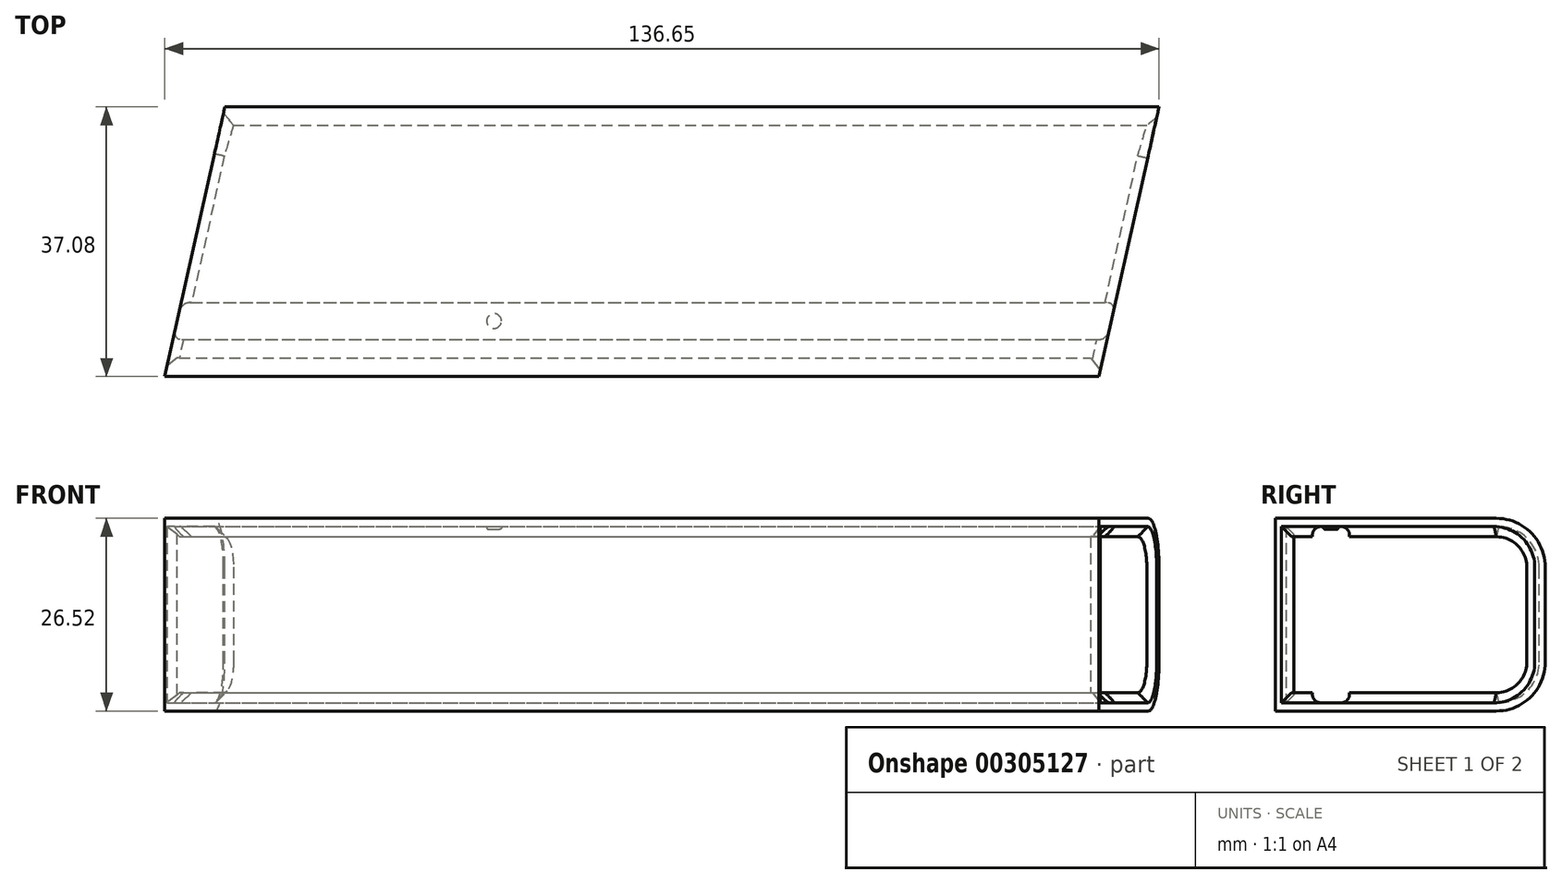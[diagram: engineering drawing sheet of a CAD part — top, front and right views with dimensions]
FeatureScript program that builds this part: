
annotation { "Feature Type Name" : "Feature", "Feature Type Description" : "" }
export const myFeature = defineFeature(function(context is Context, id is Id, definition is map)
    precondition{}
    {
        {
            var Q0;
            Q0=qCreatedBy(makeId("Top.planeOp"),FACE);
            var sketch = newSketch(context, id + "F0", { "sketchPlane" : qUnion([Q0])});
            skLineSegment(sketch, "E0.bottom", {"start": v(0, 0) * mm, "end": v(136.65, 0) * mm});
            skLineSegment(sketch, "E0.top", {"start": v(0, 37.08) * mm, "end": v(136.65, 37.08) * mm});
            skLineSegment(sketch, "E0.left", {"start": v(0, 0) * mm, "end": v(0, 37.08) * mm});
            skLineSegment(sketch, "E0.right", {"start": v(136.65, 0) * mm, "end": v(136.65, 37.08) * mm});
            skSolve(sketch);
        }
        {
            var Q0;
            Q0 = qSketchRegion(id + "F0", true);
            extrude(context, id + "F1", {"entities" : qUnion([Q0]), "depth" : 26.52 * mm});
        }
        {
            var Q0;
            Q0=makeQuery(id+"F1.opExtrude","SWEPT_FACE",FACE,{"disambiguationData":[OSD([sQuery(id+"F0.wireOp",EDGE,"E0.right")])]});
            var Q1;
            Q1=makeQuery(id+"F1.opExtrude","CAP_VERTEX",VERTEX,{"disambiguationData":[OSD([sQuery(id+"F0.wireOp",EDGE,"E0.bottom"),sQuery(id+"F0.wireOp",EDGE,"E0.right")])],"isStart":false});
            cPlane(context, id + "F2", {"entities" : qUnion([Q0, Q1]), "cplaneType" : CPlaneType.PLANE_POINT, "offset" : 25.4 * mm, "width" : 152.4 * mm, "height" : 152.4 * mm});
        }
        {
            var Q0;
            Q0=makeQuery(id+"F1.opExtrude","CAP_FACE",FACE,{"disambiguationData":[OSD([sQuery(id+"F0.wireOp",EDGE,"E0.bottom"),sQuery(id+"F0.wireOp",EDGE,"E0.top"),sQuery(id+"F0.wireOp",EDGE,"E0.left"),sQuery(id+"F0.wireOp",EDGE,"E0.right")])],"isStart":false});
            var sketch = newSketch(context, id + "F3", { "sketchPlane" : qUnion([Q0])});
            skLineSegment(sketch, "E1.0", {"start": v(0, 0) * mm, "end": v(0, 37.08) * mm});
            skLineSegment(sketch, "E2.0", {"start": v(136.65, 0) * mm, "end": v(136.65, 37.08) * mm});
            skLineSegment(sketch, "E3.0", {"start": v(0, 37.08) * mm, "end": v(136.65, 37.08) * mm, "construction": true});
            skLineSegment(sketch, "E4.0", {"start": v(0, 0) * mm, "end": v(136.65, 0) * mm, "construction": true});
            skLineSegment(sketch, "E5", {"start": v(0, 0) * mm, "end": v(8.26, 37.08) * mm});
            skLineSegment(sketch, "E6", {"start": v(8.26, 37.08) * mm, "end": v(0, 37.08) * mm});
            skLineSegment(sketch, "E7", {"start": v(136.65, 37.08) * mm, "end": v(128.4, 0) * mm});
            skLineSegment(sketch, "E8", {"start": v(128.4, 0) * mm, "end": v(136.65, 0) * mm});
            skSolve(sketch);
        }
        {
            var Q0;
            Q0 = qSketchRegion(id + "F3", true);
            extrude(context, id + "F4", {"entities" : qUnion([Q0]), "operationType" : NewBodyOperationType.REMOVE, "endBound" : BoundingType.UP_TO_NEXT, "oppositeDirection" : true, "depth" : 25.4 * mm});
        }
        {
            var Q0;
            Q0=makeQuery(id+"F1.opExtrude","CAP_EDGE",EDGE,{"disambiguationData":[OSD([sQuery(id+"F0.wireOp",EDGE,"E0.top")])],"isStart":false});
            var Q1;
            Q1=makeQuery(id+"F1.opExtrude","CAP_EDGE",EDGE,{"disambiguationData":[OSD([sQuery(id+"F0.wireOp",EDGE,"E0.top")])],"isStart":true});
            fillet(context, id + "F5", {"entities" : qUnion([Q0, Q1]), "radius" : 6.73 * mm, "tangentPropagation" : true, "allowEdgeOverflow" : false});
        }
        {
            var Q0;
            Q0=makeQuery(id+"F4.boolean.opBoolean","COPY",FACE,{"derivedFrom":makeQuery(id+"F4.opExtrude","SWEPT_FACE",FACE,{"disambiguationData":[OSD([sQuery(id+"F3.wireOp",EDGE,"E5")])]})});
            var Q1;
            Q1=makeQuery(id+"F4.boolean.opBoolean","COPY",FACE,{"derivedFrom":makeQuery(id+"F4.opExtrude","SWEPT_FACE",FACE,{"disambiguationData":[OSD([sQuery(id+"F3.wireOp",EDGE,"E7")])]})});
            shell(context, id + "F6", {"entities" : qUnion([Q0, Q1]), "thickness" : 2.54 * mm});
        }
        {
            var Q0;
            Q0=qCreatedBy(id+"F2.planeOp",FACE);
            var sketch = newSketch(context, id + "F7", { "sketchPlane" : qUnion([Q0])});
            skLineSegment(sketch, "E9.0", {"start": v(30.35, 23.98) * mm, "end": v(2.54, 23.98) * mm, "construction": true});
            skLineSegment(sketch, "E10.0", {"start": v(2.54, 2.54) * mm, "end": v(30.35, 2.54) * mm, "construction": true});
            skLineSegment(sketch, "E11.bottom", {"start": v(5.08, 23.98) * mm, "end": v(10.16, 23.98) * mm});
            skLineSegment(sketch, "E11.top", {"start": v(5.08, 25.37) * mm, "end": v(10.16, 25.37) * mm});
            skLineSegment(sketch, "E11.left", {"start": v(5.08, 25.37) * mm, "end": v(5.08, 23.98) * mm});
            skLineSegment(sketch, "E11.right", {"start": v(10.16, 25.37) * mm, "end": v(10.16, 23.98) * mm});
            skLineSegment(sketch, "E12.bottom", {"start": v(5.08, 2.54) * mm, "end": v(10.16, 2.54) * mm});
            skLineSegment(sketch, "E12.top", {"start": v(5.08, 1.14) * mm, "end": v(10.16, 1.14) * mm});
            skLineSegment(sketch, "E12.left", {"start": v(5.08, 1.14) * mm, "end": v(5.08, 2.54) * mm});
            skLineSegment(sketch, "E12.right", {"start": v(10.16, 1.14) * mm, "end": v(10.16, 2.54) * mm});
            skSolve(sketch);
        }
        {
            var Q0;
            Q0=makeQuery(id+"F7.imprint","IMPRINT",FACE,{"disambiguationData":[TD([[makeQuery(id+"F7.imprint","IMPRINT",EDGE,{"derivedFrom":sQuery(id+"F7.wireOp",EDGE,"E12.bottom")}),-1.0]])]});
            var Q1;
            Q1=makeQuery(id+"F7.imprint","IMPRINT",FACE,{"disambiguationData":[TD([[makeQuery(id+"F7.imprint","IMPRINT",EDGE,{"derivedFrom":sQuery(id+"F7.wireOp",EDGE,"E11.bottom")}),1.0]])]});
            extrude(context, id + "F8", {"entities" : qUnion([Q0, Q1]), "operationType" : NewBodyOperationType.REMOVE, "endBound" : BoundingType.THROUGH_ALL, "oppositeDirection" : true, "depth" : 25.4 * mm});
        }
        {
            var Q0;
            Q0=makeQuery(id+"F8.boolean.opBoolean","COPY",EDGE,{"derivedFrom":makeQuery(id+"F8.opExtrude","SWEPT_EDGE",EDGE,{"disambiguationData":[OSD([sQuery(id+"F7.wireOp",EDGE,"E12.top"),sQuery(id+"F7.wireOp",EDGE,"E12.left")])]})});
            var Q1;
            Q1=makeQuery(id+"F8.boolean.opBoolean","COPY",EDGE,{"derivedFrom":makeQuery(id+"F8.opExtrude","SWEPT_EDGE",EDGE,{"disambiguationData":[OSD([sQuery(id+"F7.wireOp",EDGE,"E12.top"),sQuery(id+"F7.wireOp",EDGE,"E12.right")])]})});
            var Q2;
            Q2=makeQuery(id+"F8.boolean.opBoolean","COPY",EDGE,{"derivedFrom":makeQuery(id+"F8.opExtrude","SWEPT_EDGE",EDGE,{"disambiguationData":[OSD([sQuery(id+"F7.wireOp",EDGE,"E11.top"),sQuery(id+"F7.wireOp",EDGE,"E11.left")])]})});
            var Q3;
            Q3=makeQuery(id+"F8.boolean.opBoolean","COPY",EDGE,{"derivedFrom":makeQuery(id+"F8.opExtrude","SWEPT_EDGE",EDGE,{"disambiguationData":[OSD([sQuery(id+"F7.wireOp",EDGE,"E11.top"),sQuery(id+"F7.wireOp",EDGE,"E11.right")])]})});
            fillet(context, id + "F9", {"entities" : qUnion([Q0, Q1, Q2, Q3]), "radius" : 1.14 * mm, "tangentPropagation" : true, "allowEdgeOverflow" : false});
        }
        {
            var Q0;
            {var subQ0=sQuery(id+"F3.wireOp",EDGE,"E7");Q0=makeQuery(id+"F8.boolean.opBoolean","SPLIT",EDGE,{"disambiguationData":[TD([makeQuery(id+"F8.opExtrude","SWEPT_FACE",FACE,{"disambiguationData":[OSD([sQuery(id+"F7.wireOp",EDGE,"E11.right")])]})])],"derivedFrom":makeQuery(id+"F6.opShell","OFFSET_EDGE",EDGE,{"disambiguationData":[OSD([subQ0])]})});}
            var Q1;
            {var subQ0=sQuery(id+"F3.wireOp",EDGE,"E7");var subQ1=sQuery(id+"F0.wireOp",EDGE,"E0.top");Q1=makeQuery(id+"F6.opShell","OFFSET_EDGE",EDGE,{"disambiguationData":[OSD([subQ1,subQ0]),TDD([makeQuery(id+"F5.opFillet","BLEND_EDGE",EDGE,{"blendedFrom":[makeQuery(id+"F1.opExtrude","CAP_EDGE",EDGE,{"disambiguationData":[OSD([subQ1])],"isStart":false}),makeQuery(id+"F4.boolean.opBoolean","COPY",FACE,{"derivedFrom":makeQuery(id+"F4.opExtrude","SWEPT_FACE",FACE,{"disambiguationData":[OSD([subQ0])]})})],"blendedInto":[makeQuery(id+"F4.boolean.opBoolean","COPY",FACE,{"derivedFrom":makeQuery(id+"F4.opExtrude","SWEPT_FACE",FACE,{"disambiguationData":[OSD([subQ0])]})})]})])]});}
            var Q2;
            Q2=makeQuery(id+"F6.opShell","OFFSET_EDGE",EDGE,{"disambiguationData":[OSD([sQuery(id+"F0.wireOp",EDGE,"E0.bottom"),sQuery(id+"F3.wireOp",EDGE,"E7"),sQuery(id+"F3.wireOp",EDGE,"E8")])]});
            var Q3;
            {var subQ0=sQuery(id+"F3.wireOp",EDGE,"E7");var subQ1=sQuery(id+"F0.wireOp",EDGE,"E0.bottom");var subQ2=sQuery(id+"F0.wireOp",EDGE,"E0.right");var subQ3=sQuery(id+"F0.wireOp",EDGE,"E0.left");var subQ4=sQuery(id+"F0.wireOp",EDGE,"E0.top");Q3=makeQuery(id+"F8.boolean.opBoolean","SPLIT",EDGE,{"disambiguationData":[TD([makeQuery(id+"F6.opShell","OFFSET_FACE",FACE,{"disambiguationData":[OSD([subQ1])]})])],"derivedFrom":makeQuery(id+"F6.opShell","OFFSET_EDGE",EDGE,{"disambiguationData":[OSD([subQ1,subQ4,subQ3,subQ2,subQ0])]})});}
            var Q4;
            {var subQ0=sQuery(id+"F3.wireOp",EDGE,"E7");var subQ4=sQuery(id+"F0.wireOp",EDGE,"E0.bottom");Q4=makeQuery(id+"F8.boolean.opBoolean","SPLIT",EDGE,{"disambiguationData":[TD([makeQuery(id+"F6.opShell","OFFSET_FACE",FACE,{"disambiguationData":[OSD([subQ4])]})])],"derivedFrom":makeQuery(id+"F6.opShell","OFFSET_EDGE",EDGE,{"disambiguationData":[OSD([subQ0])]})});}
            chamfer(context, id + "F10", {"entities" : qUnion([Q0, Q1, Q2, Q3, Q4]), "width" : 1.4 * mm, "tangentPropagation" : true});
        }
        {
            var Q0;
            {var subQ0=sQuery(id+"F3.wireOp",EDGE,"E5");var subQ1=sQuery(id+"F0.wireOp",EDGE,"E0.bottom");Q0=makeQuery(id+"F8.boolean.opBoolean","SPLIT",EDGE,{"disambiguationData":[TD([makeQuery(id+"F6.opShell","OFFSET_FACE",FACE,{"disambiguationData":[OSD([subQ1])]})])],"derivedFrom":makeQuery(id+"F6.opShell","OFFSET_EDGE",EDGE,{"disambiguationData":[OSD([subQ0])]})});}
            var Q1;
            {var subQ0=sQuery(id+"F3.wireOp",EDGE,"E5");Q1=makeQuery(id+"F8.boolean.opBoolean","SPLIT",EDGE,{"disambiguationData":[TD([makeQuery(id+"F8.opExtrude","SWEPT_FACE",FACE,{"disambiguationData":[OSD([sQuery(id+"F7.wireOp",EDGE,"E11.right")])]})])],"derivedFrom":makeQuery(id+"F6.opShell","OFFSET_EDGE",EDGE,{"disambiguationData":[OSD([subQ0])]})});}
            var Q2;
            {var subQ0=sQuery(id+"F3.wireOp",EDGE,"E5");var subQ1=sQuery(id+"F0.wireOp",EDGE,"E0.right");var subQ2=sQuery(id+"F0.wireOp",EDGE,"E0.left");var subQ3=sQuery(id+"F0.wireOp",EDGE,"E0.top");var subQ4=sQuery(id+"F0.wireOp",EDGE,"E0.bottom");Q2=makeQuery(id+"F8.boolean.opBoolean","SPLIT",EDGE,{"disambiguationData":[TD([makeQuery(id+"F6.opShell","OFFSET_FACE",FACE,{"disambiguationData":[OSD([subQ4])]})])],"derivedFrom":makeQuery(id+"F6.opShell","OFFSET_EDGE",EDGE,{"disambiguationData":[OSD([subQ4,subQ3,subQ2,subQ1,subQ0])]})});}
            var Q3;
            Q3=makeQuery(id+"F6.opShell","OFFSET_EDGE",EDGE,{"disambiguationData":[OSD([sQuery(id+"F0.wireOp",EDGE,"E0.bottom"),sQuery(id+"F0.wireOp",EDGE,"E0.left"),sQuery(id+"F3.wireOp",EDGE,"E1.0"),sQuery(id+"F3.wireOp",EDGE,"E5")])]});
            chamfer(context, id + "F11", {"entities" : qUnion([Q0, Q1, Q2, Q3]), "width" : 1.4 * mm, "tangentPropagation" : true});
        }
        {
            var Q0;
            Q0=makeQuery(id+"F8.boolean.opBoolean","COPY",FACE,{"derivedFrom":makeQuery(id+"F8.opExtrude","SWEPT_FACE",FACE,{"disambiguationData":[OSD([sQuery(id+"F7.wireOp",EDGE,"E11.top")])]})});
            var sketch = newSketch(context, id + "F12", { "sketchPlane" : qUnion([Q0])});
            skCircle(sketch, "E13", {"center": v(45.26, -7.62) * mm, "radius": 1.02 * mm});
            skPoint(sketch, "E14.0", {"position": v(1.7, -7.62) * mm});
            skPoint(sketch, "E15.0", {"position": v(130.1, -7.62) * mm});
            skLineSegment(sketch, "E16", {"start": v(130.1, -7.62) * mm, "end": v(1.7, -7.62) * mm, "construction": true});
            skSolve(sketch);
        }
        {
            var Q0;
            Q0 = qSketchRegion(id + "F12", true);
            extrude(context, id + "F13", {"entities" : qUnion([Q0]), "operationType" : NewBodyOperationType.ADD, "depth" : 0.38 * mm});
        }
        {
            var Q0;
            Q0=makeQuery(id+"F13.opExtrude","CAP_EDGE",EDGE,{"disambiguationData":[OSD([sQuery(id+"F12.wireOp",EDGE,"E13")])],"isStart":false});
            fillet(context, id + "F14", {"entities" : qUnion([Q0]), "radius" : 0.25 * mm, "tangentPropagation" : true, "allowEdgeOverflow" : false});
        }
    });
